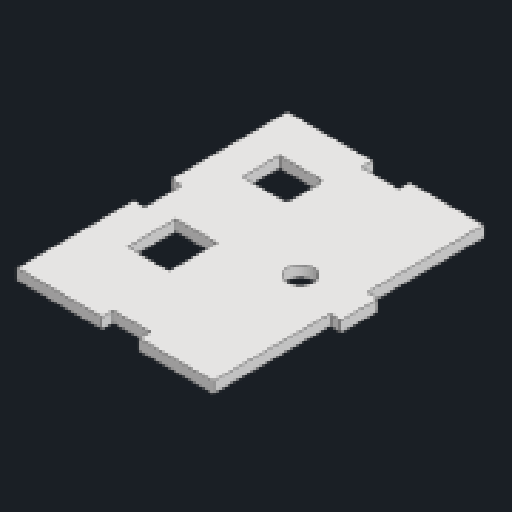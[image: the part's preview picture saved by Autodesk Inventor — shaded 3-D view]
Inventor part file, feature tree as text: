
AUTODESK INVENTOR PART (.ipt)
format: ipt  version: 2023 (Build 270158000, 158)  size: 178,688 bytes
history: native  units: mm
features: reference x9, extrude x6, other x6, sketch x5
ambient origin geometry x8: Origin, YZ Plane, XZ Plane, XY Plane, X Axis, Y Axis, Z Axis, Center Point
bodies: Solid1 (feature_tree)
feature tree (26):
  extrude  "Extrusion1"  Depth=56.0mm
  extrude  "Extrusion3"  TaperAngle=0.0deg  [1 undecoded]
  extrude  "Extrusion4"  Depth=16.0mm
  extrude  "Extrusion7"  Depth=10.0mm
  sketch  "Sketch9"  dims[d27=3.0mm d28=10.0mm d29=3.0mm d30=3.0mm d31=10.0mm d32=3.0mm d33=10.0mm d34=0.0mm d35=0.0mm d36=36.5mm d38=0.5mm d39=0.5mm d41=3.0mm d42=0.0mm d43=0.0mm d44=0.0mm]
  extrude  "Extrusion8"  Depth=10.0mm
  extrude  "Extrusion9"  Depth=3.0mm
  sketch  "Sketch1"  dims[d0=73.0mm d1=56.0mm]
  sketch  "Sketch3"  dims[d2=3.0mm d3=0.0mm d10=0.0mm d11=0.0mm]
  sketch  "Sketch4"  dims[d12=7.0mm d13=16.0mm]
  sketch  "Sketch7"  dims[d14=0.0mm d15=0.0mm d26=10.0mm]
  reference  "Reference14"
  reference  "Reference15"
  reference  "Reference16"
  reference  "Reference17"
  reference  "Reference18"
  reference  "Reference19"
  reference  "Reference20"
  reference  "Reference21"
  reference  "Reference22"
  parser-record x1  (decoder bookkeeping rows leaked as tree rows — omitted from the tree; the rows remain in map.json)
  other  "AlarmClock.iam"
  other  "arduino uno:1"
  other  "USB type b.SLDPRT_3"
  other  "USB SHELL_82"
  other  "power jack_4"
note: 1 required parameter value undecoded (feature->parameter linkage not recoverable at this tier; creation-order binding heuristic only, values carry confidence <= 0.55)
note: 1 file-system path scrubbed to <path> (originals preserved in map.json)
